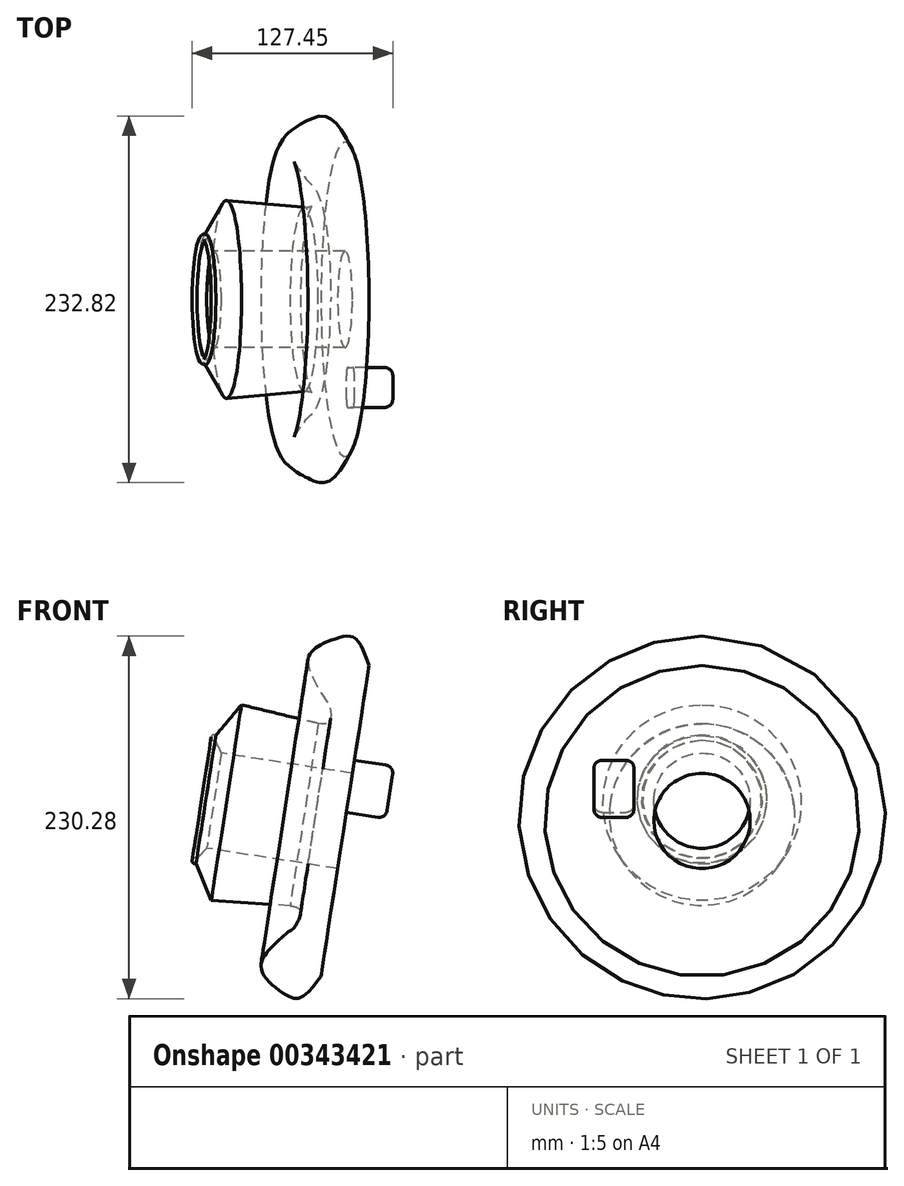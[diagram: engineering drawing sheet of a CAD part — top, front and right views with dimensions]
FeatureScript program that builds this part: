
annotation { "Feature Type Name" : "Feature", "Feature Type Description" : "" }
export const myFeature = defineFeature(function(context is Context, id is Id, definition is map)
    precondition{}
    {
        {
            var Q0;
            Q0=qCreatedBy(makeId("Front.planeOp"),FACE);
            var sketch = newSketch(context, id + "F0", { "sketchPlane" : qUnion([Q0])});
            skLineSegment(sketch, "E0", {"start": v(-41.8, 50.13) * mm, "end": v(-47.88, 43.36) * mm});
            skLineSegment(sketch, "E1", {"start": v(-48.56, 40.43) * mm, "end": v(-38.86, 16.98) * mm});
            skLineSegment(sketch, "E2", {"start": v(-38.86, 16.98) * mm, "end": v(11.19, 13.6) * mm});
            skLineSegment(sketch, "E3", {"start": v(41.4, 37.28) * mm, "end": v(-41.8, 50.13) * mm});
            skArc(sketch, "E4", {"start": v(-47.88, 43.36) * mm, "mid": v(-51, 42.54) * mm, "end": v(-48.56, 40.43) * mm});
            skLineSegment(sketch, "E5", {"start": v(6.97, 73.53) * mm, "end": v(43.43, 67.9) * mm, "construction": true});
            skLineSegment(sketch, "E6", {"start": v(41.4, 37.28) * mm, "end": v(30.82, -31.21) * mm});
            skFitSpline(sketch, "E7", {"points": [v(30.82, -31.21) * mm, v(16.97, -45.1) * mm, v(8.18, -42.84) * mm, v(-2.42, -34.5) * mm, v(-6.48, -28.64) * mm, v(-7.15, -22.55) * mm, v(0, -12.18) * mm, v(11.11, -2.26) * mm, v(14.04, 0) * mm, v(17.65, 10.37) * mm, v(11.19, 13.6) * mm], "startDerivative": vector(-101.65, -133.67) * mm, "endDerivative": vector(-102.64, 17.46) * mm});
            skSolve(sketch);
        }
        {
            var Q0;
            Q0=makeQuery(id+"F0.imprint","IMPRINT",FACE,{"disambiguationData":[TD([[makeQuery(id+"F0.imprint","IMPRINT",EDGE,{"derivedFrom":sQuery(id+"F0.wireOp",EDGE,"E0")}),1.0]])]});
            var Q1;
            Q1=sQuery(id+"F0.wireOp",EDGE,"E2");
            var Q2;
            Q2=sQuery(id+"F0.wireOp",EDGE,"WhQWkSNY-SD11-AK0K-kFDv-CDoIlbfsV9Ka");
            var Q3;
            Q3=sQuery(id+"F0.wireOp",EDGE,"E2yNqJkC-XHC7-VEzD-06Zk-s43XcbBB7KFo");
            var Q4;
            Q4=sQuery(id+"F0.wireOp",EDGE,"4vhd2kPl-NkFs-kUOo-PYiH-PN9hthZMxVtn");
            var Q5;
            Q5=sQuery(id+"F0.wireOp",EDGE,"DJk6MFf1-ebrE-iMAg-zwqw-QWTDwASv6WkM");
            var Q6;
            Q6=sQuery(id+"F0.wireOp",EDGE,"E1");
            var Q7;
            Q7=sQuery(id+"F0.wireOp",EDGE,"SMrMcPzC-3vbh-2uSQ-iXRu-S4ZGepco0VFK");
            var Q8;
            Q8=sQuery(id+"F0.wireOp",EDGE,"E3");
            var Q9;
            Q9=sQuery(id+"F0.wireOp",EDGE,"E4");
            var Q10;
            Q10=sQuery(id+"F0.wireOp",EDGE,"E0");
            var Q11;
            Q11=sQuery(id+"F0.wireOp",EDGE,"E5");
            revolve(context, id + "F1", {"entities" : qUnion([Q0]), "surfaceEntities" : qUnion([Q1, Q2, Q3, Q4, Q5, Q6, Q7, Q8, Q9, Q10]), "axis" : qUnion([Q11]), "revolveType" : RevolveType.FULL});
        }
        {
            var Q0;
            Q0=makeQuery(id+"F1.opRevolve","SWEPT_FACE",FACE,{"disambiguationData":[OSD([sQuery(id+"F0.wireOp",EDGE,"E6")])]});
            var sketch = newSketch(context, id + "F2", { "sketchPlane" : qUnion([Q0])});
            skLineSegment(sketch, "E8.bottom", {"start": v(-68.6, 79.2) * mm, "end": v(-43.29, 79.2) * mm});
            skLineSegment(sketch, "E8.top", {"start": v(-68.6, 112.73) * mm, "end": v(-43.29, 112.73) * mm});
            skLineSegment(sketch, "E8.left", {"start": v(-68.6, 79.2) * mm, "end": v(-68.6, 112.73) * mm});
            skLineSegment(sketch, "E8.right", {"start": v(-43.29, 79.2) * mm, "end": v(-43.29, 112.73) * mm});
            skSolve(sketch);
        }
        {
            var Q0;
            Q0 = qSketchRegion(id + "F2", true);
            extrude(context, id + "F3", {"entities" : qUnion([Q0]), "operationType" : NewBodyOperationType.ADD, "depth" : 25.4 * mm});
        }
        {
            var Q0;
            Q0=makeQuery(id+"F3.opExtrude","CAP_EDGE",EDGE,{"disambiguationData":[OSD([sQuery(id+"F2.wireOp",EDGE,"E8.left")])],"isStart":false});
            var Q1;
            Q1=makeQuery(id+"F3.opExtrude","CAP_EDGE",EDGE,{"disambiguationData":[OSD([sQuery(id+"F2.wireOp",EDGE,"E8.right")])],"isStart":false});
            var Q2;
            Q2=makeQuery(id+"F3.opExtrude","CAP_EDGE",EDGE,{"disambiguationData":[OSD([sQuery(id+"F2.wireOp",EDGE,"E8.bottom")])],"isStart":false});
            var Q3;
            Q3=makeQuery(id+"F3.opExtrude","CAP_EDGE",EDGE,{"disambiguationData":[OSD([sQuery(id+"F2.wireOp",EDGE,"E8.top")])],"isStart":false});
            var Q4;
            Q4=makeQuery(id+"F3.opExtrude","SWEPT_EDGE",EDGE,{"disambiguationData":[OSD([sQuery(id+"F2.wireOp",EDGE,"E8.top"),sQuery(id+"F2.wireOp",EDGE,"E8.left")])]});
            var Q5;
            Q5=makeQuery(id+"F3.opExtrude","SWEPT_EDGE",EDGE,{"disambiguationData":[OSD([sQuery(id+"F2.wireOp",EDGE,"E8.bottom"),sQuery(id+"F2.wireOp",EDGE,"E8.left")])]});
            var Q6;
            Q6=makeQuery(id+"F3.opExtrude","SWEPT_EDGE",EDGE,{"disambiguationData":[OSD([sQuery(id+"F2.wireOp",EDGE,"E8.bottom"),sQuery(id+"F2.wireOp",EDGE,"E8.right")])]});
            var Q7;
            Q7=makeQuery(id+"F3.opExtrude","SWEPT_EDGE",EDGE,{"disambiguationData":[OSD([sQuery(id+"F2.wireOp",EDGE,"E8.top"),sQuery(id+"F2.wireOp",EDGE,"E8.right")])]});
            var Q8;
            Q8=makeQuery(id+"F3.opExtrude","CAP_EDGE",EDGE,{"disambiguationData":[OSD([sQuery(id+"F2.wireOp",EDGE,"E8.top")])],"isStart":true});
            var Q9;
            Q9=makeQuery(id+"F3.opExtrude","CAP_EDGE",EDGE,{"disambiguationData":[OSD([sQuery(id+"F2.wireOp",EDGE,"E8.right")])],"isStart":true});
            var Q10;
            Q10=makeQuery(id+"F3.opExtrude","CAP_EDGE",EDGE,{"disambiguationData":[OSD([sQuery(id+"F2.wireOp",EDGE,"E8.bottom")])],"isStart":true});
            var Q11;
            Q11=makeQuery(id+"F3.opExtrude","CAP_EDGE",EDGE,{"disambiguationData":[OSD([sQuery(id+"F2.wireOp",EDGE,"E8.left")])],"isStart":true});
            fillet(context, id + "F4", {"entities" : qUnion([Q0, Q1, Q2, Q3, Q4, Q5, Q6, Q7, Q8, Q9, Q10, Q11]), "radius" : 5.08 * mm, "tangentPropagation" : true, "allowEdgeOverflow" : false});
        }
    });
